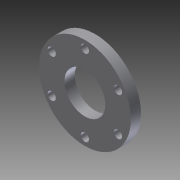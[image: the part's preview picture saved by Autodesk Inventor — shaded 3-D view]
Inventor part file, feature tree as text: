
AUTODESK INVENTOR PART (.ipt)
format: ipt  version: 2012 (Build 160160000, 160)  size: 94,208 bytes
history: native  units: in
note: dims shown in document units (in); Inventor stores cm internally (conversion verified against a paired STEP export)
features: sketch x1, extrude x1, hole x1
ambient origin geometry x8: Origin, YZ Plane, XZ Plane, XY Plane, X Axis, Y Axis, Z Axis, Center Point
bodies: Solid1 (feature_tree)
feature tree (3):
  sketch  "Sketch1"  dims[d0=2.25in d1=1.875in d2=2.3622in d4=360.0deg d6=1.0in d7=0.25in d8=0.0in d9=0.2in d10=0.75in d11=0.375in d12=0.25in d13=0.5635in d14=1.0in d15=0.8108in]
  extrude  "Extrusion1"  Depth=1.875in
  hole  "Hole1"  [1 undecoded]
note: 1 required parameter value undecoded (feature->parameter linkage not recoverable at this tier; creation-order binding heuristic only, values carry confidence <= 0.55)
